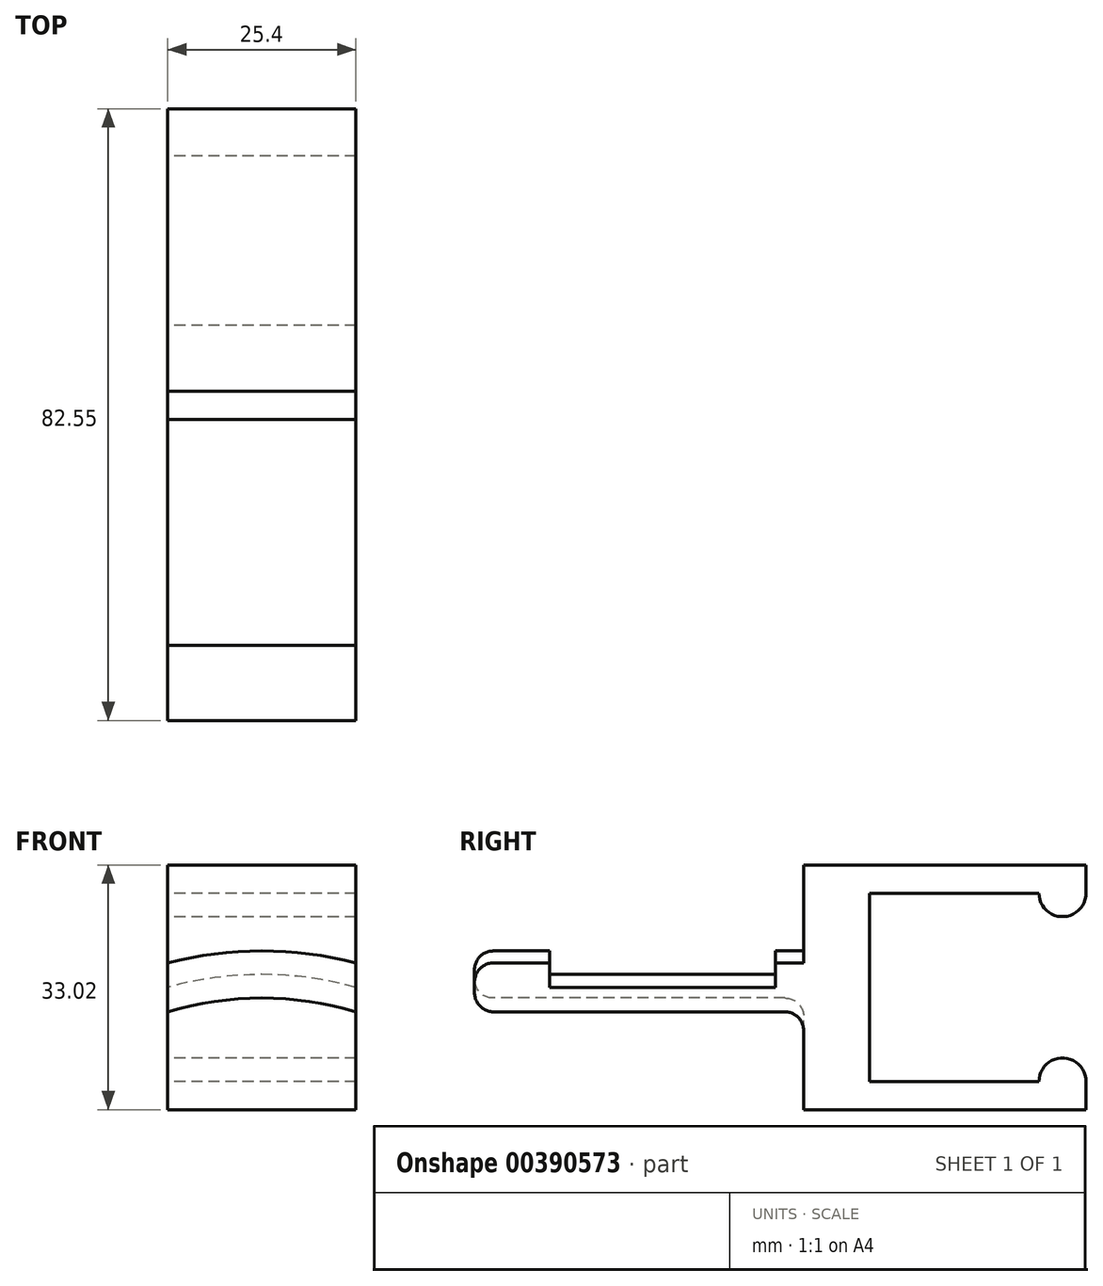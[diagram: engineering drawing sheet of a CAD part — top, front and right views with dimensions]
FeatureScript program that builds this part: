
annotation { "Feature Type Name" : "Feature", "Feature Type Description" : "" }
export const myFeature = defineFeature(function(context is Context, id is Id, definition is map)
    precondition{}
    {
        {
            var Q0;
            Q0=qCreatedBy(makeId("Front.planeOp"),FACE);
            var sketch = newSketch(context, id + "F0", { "sketchPlane" : qUnion([Q0])});
            skCircle(sketch, "E0", {"center": v(0, 0) * mm, "radius": 50.8 * mm});
            skCircle(sketch, "E1", {"center": v(0, 0) * mm, "radius": 44.45 * mm});
            skLineSegment(sketch, "E2", {"start": v(0, 0) * mm, "end": v(34.96, 60.55) * mm});
            skLineSegment(sketch, "E3", {"start": v(0, 0) * mm, "end": v(-33.43, 57.9) * mm});
            skCircle(sketch, "E4", {"center": v(0, 0) * mm, "radius": 47.63 * mm});
            skSolve(sketch);
        }
        {
            var Q0;
            {var subQ0=sQuery(id+"F0.wireOp",EDGE,"E2");var subQ1=sQuery(id+"F0.wireOp",EDGE,"E0");var subQ2=makeQuery(id+"F0.imprint","INTERSECT",VERTEX,{"derivedFrom":[subQ1,subQ0]});Q0=makeQuery(id+"F0.imprint","IMPRINT",FACE,{"disambiguationData":[TD([[makeQuery(id+"F0.imprint","IMPRINT",EDGE,{"disambiguationData":[TD([[subQ2,-1.0]])],"derivedFrom":subQ1}),1.0]])]});}
            extrude(context, id + "F1", {"entities" : qUnion([Q0]), "oppositeDirection" : true, "depth" : 10.16 * mm});
        }
        {
            var Q0;
            {var subQ0=sQuery(id+"F0.wireOp",EDGE,"E2");var subQ1=sQuery(id+"F0.wireOp",EDGE,"E1");var subQ2=makeQuery(id+"F0.imprint","INTERSECT",VERTEX,{"derivedFrom":[subQ1,subQ0]});Q0=makeQuery(id+"F0.imprint","IMPRINT",FACE,{"disambiguationData":[TD([[makeQuery(id+"F0.imprint","IMPRINT",EDGE,{"disambiguationData":[TD([[subQ2,-1.0]])],"derivedFrom":subQ1}),-1.0]])]});}
            extrude(context, id + "F2", {"entities" : qUnion([Q0]), "operationType" : NewBodyOperationType.ADD, "oppositeDirection" : true, "depth" : 50.8 * mm});
        }
        {
            var Q0;
            Q0=makeQuery(id+"F2.opExtrude","CAP_FACE",FACE,{"disambiguationData":[OSD([sQuery(id+"F0.wireOp",EDGE,"E1"),sQuery(id+"F0.wireOp",EDGE,"E2"),sQuery(id+"F0.wireOp",EDGE,"E3"),sQuery(id+"F0.wireOp",EDGE,"E4")])],"isStart":false});
            var sketch = newSketch(context, id + "F3", { "sketchPlane" : qUnion([Q0])});
            skCircle(sketch, "E5", {"center": v(0, 0) * mm, "radius": 50.8 * mm});
            skCircle(sketch, "E6", {"center": v(0, 0) * mm, "radius": 47.63 * mm});
            skLineSegment(sketch, "E7", {"start": v(0, 0) * mm, "end": v(39.48, 68.37) * mm});
            skLineSegment(sketch, "E8", {"start": v(0, 0) * mm, "end": v(-37.6, 65.13) * mm});
            skLineSegment(sketch, "E9", {"start": v(12.7, 45.9) * mm, "end": v(12.7, 64.95) * mm});
            skLineSegment(sketch, "E10", {"start": v(12.7, 64.95) * mm, "end": v(-12.7, 64.95) * mm});
            skLineSegment(sketch, "E11", {"start": v(-12.7, 64.95) * mm, "end": v(-12.7, 26.85) * mm});
            skLineSegment(sketch, "E12", {"start": v(-12.7, 26.85) * mm, "end": v(12.7, 26.85) * mm});
            skLineSegment(sketch, "E13", {"start": v(12.7, 45.9) * mm, "end": v(12.7, 26.85) * mm});
            skSolve(sketch);
        }
        {
            var Q0;
            {var subQ5=sQuery(id+"F3.wireOp",EDGE,"E6");Q0=makeQuery(id+"F3.imprint","IMPRINT",FACE,{"disambiguationData":[TD([[makeQuery(id+"F3.imprint","IMPRINT",EDGE,{"disambiguationData":[OD(0.0)],"derivedFrom":subQ5}),1.0]])]});}
            extrude(context, id + "F4", {"entities" : qUnion([Q0]), "operationType" : NewBodyOperationType.ADD, "oppositeDirection" : true, "depth" : 10.16 * mm});
        }
        {
            var Q0;
            {var subQ5=sQuery(id+"F3.wireOp",EDGE,"E10");Q0=makeQuery(id+"F3.imprint","IMPRINT",FACE,{"disambiguationData":[TD([[makeQuery(id+"F3.imprint","IMPRINT",EDGE,{"derivedFrom":subQ5}),1.0]])]});}
            var Q1;
            {var subQ0=sQuery(id+"F3.wireOp",EDGE,"E12");Q1=makeQuery(id+"F3.imprint","IMPRINT",FACE,{"disambiguationData":[TD([[makeQuery(id+"F3.imprint","IMPRINT",EDGE,{"derivedFrom":subQ0}),1.0]])]});}
            var Q2;
            {var subQ1=sQuery(id+"F3.wireOp",EDGE,"E9");var subQ5=sQuery(id+"F3.wireOp",EDGE,"E6");var subQ6=makeQuery(id+"F3.imprint","INTERSECT",VERTEX,{"derivedFrom":[subQ5,subQ1]});var subQ7=sQuery(id+"F3.wireOp",EDGE,"E11");var subQ8=makeQuery(id+"F3.imprint","INTERSECT",VERTEX,{"derivedFrom":[subQ5,subQ7]});Q2=makeQuery(id+"F3.imprint","IMPRINT",FACE,{"disambiguationData":[TD([[makeQuery(id+"F3.imprint","IMPRINT",EDGE,{"disambiguationData":[TD([[subQ8,-1.0],[subQ6,1.0]])],"derivedFrom":subQ5}),-1.0]])]});}
            var Q3;
            {var subQ0=sQuery(id+"F3.wireOp",EDGE,"E9");var subQ1=sQuery(id+"F3.wireOp",EDGE,"E5");var subQ2=makeQuery(id+"F3.imprint","INTERSECT",VERTEX,{"derivedFrom":[subQ1,subQ0]});Q3=makeQuery(id+"F3.imprint","IMPRINT",FACE,{"disambiguationData":[TD([[makeQuery(id+"F3.imprint","IMPRINT",EDGE,{"disambiguationData":[TD([[subQ2,-1.0]])],"derivedFrom":subQ1}),1.0]])]});}
            extrude(context, id + "F5", {"entities" : qUnion([Q0, Q1, Q2, Q3]), "operationType" : NewBodyOperationType.ADD, "endBound" : BoundingType.SYMMETRIC, "depth" : 12.7 * mm});
        }
        {
            var Q0;
            Q0=makeQuery(id+"F5.opExtrude","CAP_FACE",FACE,{"disambiguationData":[OSD([sQuery(id+"F3.wireOp",EDGE,"E9"),sQuery(id+"F3.wireOp",EDGE,"E10"),sQuery(id+"F3.wireOp",EDGE,"E11"),sQuery(id+"F3.wireOp",EDGE,"E12"),sQuery(id+"F3.wireOp",EDGE,"E13")])],"isStart":false});
            extrude(context, id + "F6", {"entities" : qUnion([Q0]), "operationType" : NewBodyOperationType.ADD, "depth" : 25.4 * mm});
        }
        {
            var Q0;
            {var subQ0=sQuery(id+"F3.wireOp",EDGE,"E13");var subQ1=sQuery(id+"F3.wireOp",EDGE,"E9");Q0=makeQuery(id+"F6.boolean.opBoolean","MERGE",FACE,{"derivedFrom":[makeQuery(id+"F5.opExtrude","SWEPT_FACE",FACE,{"disambiguationData":[OSD([subQ1,subQ0])]}),makeQuery(id+"F6.opExtrude","SWEPT_FACE",FACE,{"disambiguationData":[OSD([subQ1,subQ0])]})]});}
            var sketch = newSketch(context, id + "F7", { "sketchPlane" : qUnion([Q0])});
            skLineSegment(sketch, "E14", {"start": v(0, 0) * mm, "end": v(-82.55, 0) * mm});
            skLineSegment(sketch, "E15", {"start": v(-82.55, 0) * mm, "end": v(-82.55, 45.9) * mm});
            skLineSegment(sketch, "E16", {"start": v(-82.55, 45.9) * mm, "end": v(-53.34, 45.9) * mm});
            skLineSegment(sketch, "E17.bottom", {"start": v(-82.55, 64.95) * mm, "end": v(-44.45, 64.95) * mm});
            skLineSegment(sketch, "E17.top", {"start": v(-82.55, 26.85) * mm, "end": v(-44.45, 26.85) * mm});
            skLineSegment(sketch, "E17.left", {"start": v(-82.55, 64.95) * mm, "end": v(-82.55, 26.85) * mm});
            skLineSegment(sketch, "E17.right", {"start": v(-44.45, 64.95) * mm, "end": v(-44.45, 26.85) * mm});
            skLineSegment(sketch, "E18", {"start": v(-53.34, 45.9) * mm, "end": v(-53.34, 58.6) * mm});
            skLineSegment(sketch, "E19", {"start": v(-53.34, 58.6) * mm, "end": v(-82.55, 58.6) * mm});
            skCircle(sketch, "E20", {"center": v(-79.38, 58.6) * mm, "radius": 3.18 * mm});
            skCircle(sketch, "E21.MirrorC", {"center": v(-79.38, 33.2) * mm, "radius": 3.18 * mm});
            skLineSegment(sketch, "E22.MirrorCS", {"start": v(-53.34, 33.2) * mm, "end": v(-82.55, 33.2) * mm});
            skLineSegment(sketch, "E23.MirrorCS", {"start": v(-53.34, 45.9) * mm, "end": v(-53.34, 33.2) * mm});
            skSolve(sketch);
        }
        {
            var Q0;
            {var subQ4=sQuery(id+"F7.wireOp",EDGE,"E16");Q0=makeQuery(id+"F7.imprint","IMPRINT",FACE,{"disambiguationData":[TD([[makeQuery(id+"F7.imprint","IMPRINT",EDGE,{"derivedFrom":subQ4}),1.0]])]});}
            var Q1;
            {var subQ6=sQuery(id+"F7.wireOp",EDGE,"E16");Q1=makeQuery(id+"F7.imprint","IMPRINT",FACE,{"disambiguationData":[TD([[makeQuery(id+"F7.imprint","IMPRINT",EDGE,{"derivedFrom":subQ6}),-1.0]])]});}
            extrude(context, id + "F8", {"entities" : qUnion([Q0, Q1]), "operationType" : NewBodyOperationType.REMOVE, "oppositeDirection" : true, "depth" : 25.4 * mm});
        }
        {
            var Q0;
            Q0=makeQuery(id+"F1.opExtrude","CAP_EDGE",EDGE,{"disambiguationData":[OSD([sQuery(id+"F0.wireOp",EDGE,"E0")])],"isStart":true});
            var Q1;
            Q1=makeQuery(id+"F5.opExtrude","CAP_EDGE",EDGE,{"disambiguationData":[OSD([sQuery(id+"F3.wireOp",EDGE,"E10")])],"isStart":true});
            var Q2;
            Q2=makeQuery(id+"F6.opExtrude","CAP_EDGE",EDGE,{"disambiguationData":[OSD([sQuery(id+"F3.wireOp",EDGE,"E10")])],"isStart":false});
            var Q3;
            Q3=makeQuery(id+"F6.opExtrude","CAP_EDGE",EDGE,{"disambiguationData":[OSD([sQuery(id+"F3.wireOp",EDGE,"E12")])],"isStart":false});
            var Q4;
            Q4=makeQuery(id+"F5.opExtrude","CAP_EDGE",EDGE,{"disambiguationData":[OSD([sQuery(id+"F3.wireOp",EDGE,"E12")])],"isStart":true});
            var Q5;
            Q5=makeQuery(id+"F5.boolean.opBoolean","INTERSECT",EDGE,{"derivedFrom":[makeQuery(id+"F2.opExtrude","SWEPT_FACE",FACE,{"disambiguationData":[OSD([sQuery(id+"F0.wireOp",EDGE,"E1")])]}),makeQuery(id+"F5.opExtrude","CAP_FACE",FACE,{"disambiguationData":[OSD([sQuery(id+"F3.wireOp",EDGE,"E9"),sQuery(id+"F3.wireOp",EDGE,"E10"),sQuery(id+"F3.wireOp",EDGE,"E11"),sQuery(id+"F3.wireOp",EDGE,"E12"),sQuery(id+"F3.wireOp",EDGE,"E13")])],"isStart":true})]});
            var Q6;
            Q6=makeQuery(id+"F2.opExtrude","CAP_EDGE",EDGE,{"disambiguationData":[OSD([sQuery(id+"F0.wireOp",EDGE,"E1")])],"isStart":true});
            var Q7;
            Q7=makeQuery(id+"F2.opExtrude","SWEPT_EDGE",EDGE,{"disambiguationData":[OSD([sQuery(id+"F0.wireOp",EDGE,"E1"),sQuery(id+"F0.wireOp",EDGE,"E3")])]});
            var Q8;
            Q8=makeQuery(id+"F2.opExtrude","SWEPT_EDGE",EDGE,{"disambiguationData":[OSD([sQuery(id+"F0.wireOp",EDGE,"E1"),sQuery(id+"F0.wireOp",EDGE,"E2")])]});
            fillet(context, id + "F9", {"entities" : qUnion([Q0, Q1, Q2, Q3, Q4, Q5, Q6, Q7, Q8]), "radius" : 2.54 * mm, "tangentPropagation" : true, "allowEdgeOverflow" : false});
        }
        {
            var Q0;
            {var subQ0=sQuery(id+"F3.wireOp",EDGE,"E10");var subQ1=sQuery(id+"F3.wireOp",EDGE,"E13");var subQ2=sQuery(id+"F3.wireOp",EDGE,"E9");var subQ3=sQuery(id+"F3.wireOp",EDGE,"E11");Q0=makeQuery(id+"F5.boolean.opBoolean","SPLIT",FACE,{"disambiguationData":[TD([makeQuery(id+"F4.opExtrude","SWEPT_FACE",FACE,{"disambiguationData":[OSD([sQuery(id+"F3.wireOp",EDGE,"E5")])]})])],"derivedFrom":makeQuery(id+"F5.opExtrude","CAP_FACE",FACE,{"disambiguationData":[OSD([subQ2,subQ0,subQ3,sQuery(id+"F3.wireOp",EDGE,"E12"),subQ1])],"isStart":true})});}
            var sketch = newSketch(context, id + "F10", { "sketchPlane" : qUnion([Q0])});
            skLineSegment(sketch, "E24.bottom", {"start": v(-12.7, 62.41) * mm, "end": v(12.7, 62.41) * mm});
            skLineSegment(sketch, "E24.top", {"start": v(-12.7, 29.4) * mm, "end": v(12.7, 29.4) * mm});
            skLineSegment(sketch, "E24.left", {"start": v(-12.7, 62.41) * mm, "end": v(-12.7, 29.4) * mm});
            skLineSegment(sketch, "E24.right", {"start": v(12.7, 62.41) * mm, "end": v(12.7, 29.4) * mm});
            skLineSegment(sketch, "E25.bottom", {"start": v(-36.88, 85.37) * mm, "end": v(46.52, 85.37) * mm});
            skLineSegment(sketch, "E25.top", {"start": v(-36.88, 5.4) * mm, "end": v(46.52, 5.4) * mm});
            skLineSegment(sketch, "E25.left", {"start": v(-36.88, 85.37) * mm, "end": v(-36.88, 5.4) * mm});
            skLineSegment(sketch, "E25.right", {"start": v(46.52, 85.37) * mm, "end": v(46.52, 5.4) * mm});
            skSolve(sketch);
        }
        {
            var Q0;
            {var subQ2=sQuery(id+"F10.wireOp",EDGE,"E24.bottom");Q0=makeQuery(id+"F10.imprint","IMPRINT",FACE,{"disambiguationData":[TD([[makeQuery(id+"F10.imprint","IMPRINT",EDGE,{"derivedFrom":subQ2}),-1.0]])]});}
            extrude(context, id + "F11", {"entities" : qUnion([Q0]), "operationType" : NewBodyOperationType.REMOVE, "endBound" : BoundingType.SYMMETRIC, "oppositeDirection" : true, "depth" : 127 * mm});
        }
    });
